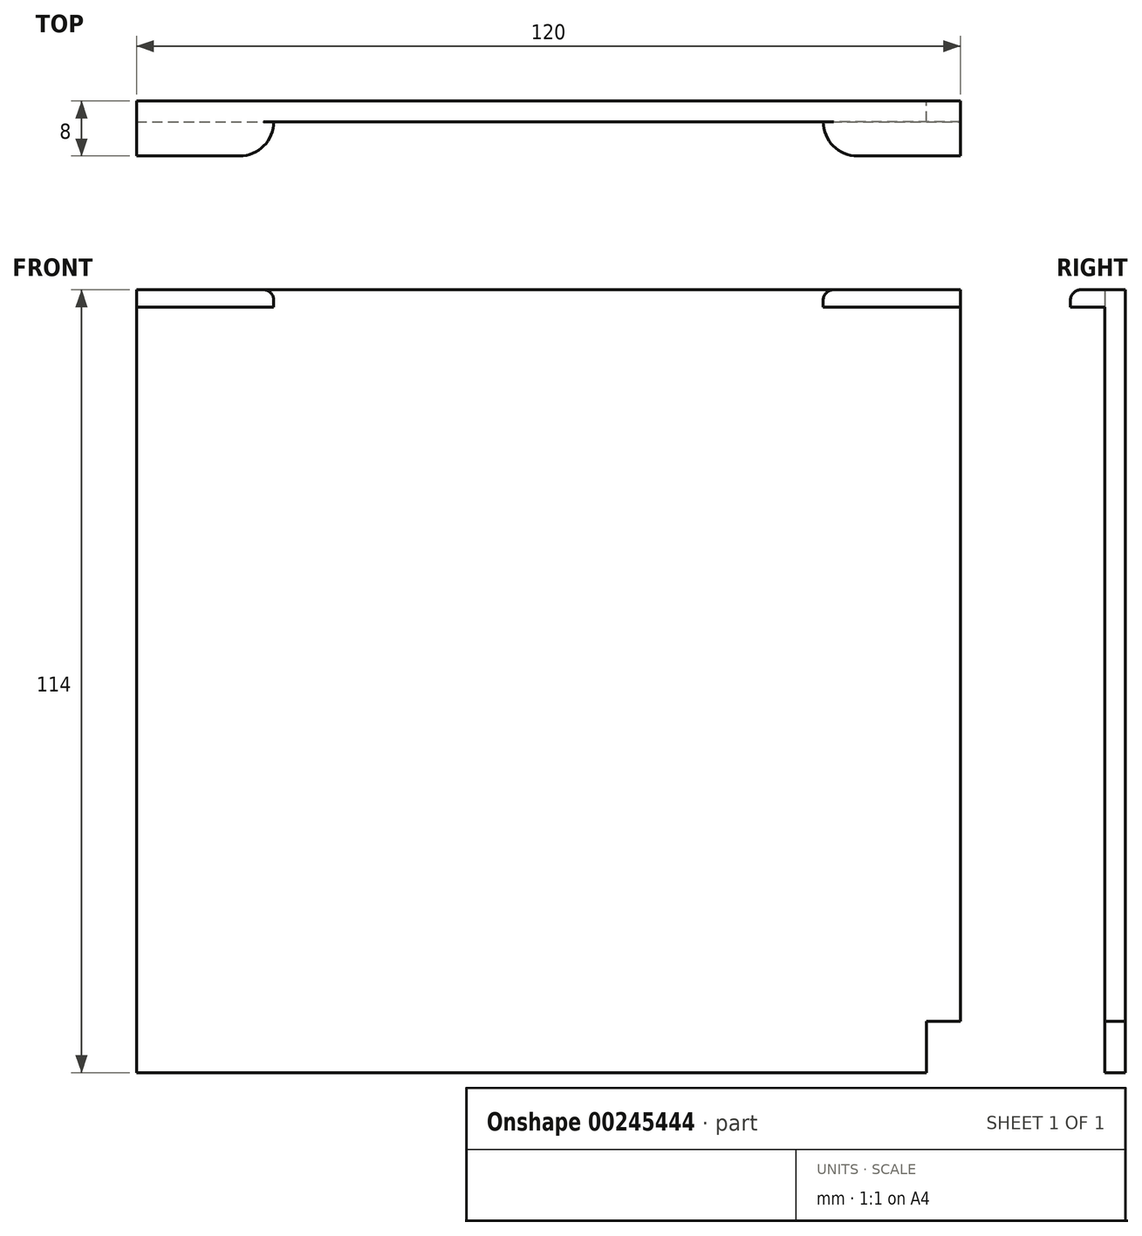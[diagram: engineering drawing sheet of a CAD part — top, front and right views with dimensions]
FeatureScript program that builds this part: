
annotation { "Feature Type Name" : "Feature", "Feature Type Description" : "" }
export const myFeature = defineFeature(function(context is Context, id is Id, definition is map)
    precondition{}
    {
        {
            var Q0;
            Q0=qCreatedBy(makeId("Front.planeOp"),FACE);
            var sketch = newSketch(context, id + "F0", { "sketchPlane" : qUnion([Q0])});
            skLineSegment(sketch, "E0.bottom", {"start": v(0, 0) * mm, "end": v(120, 0) * mm});
            skLineSegment(sketch, "E0.top", {"start": v(0, 114) * mm, "end": v(120, 114) * mm});
            skLineSegment(sketch, "E0.left", {"start": v(0, 0) * mm, "end": v(0, 114) * mm});
            skLineSegment(sketch, "E0.right", {"start": v(120, 0) * mm, "end": v(120, 114) * mm});
            skSolve(sketch);
        }
        {
            var Q0;
            Q0=qSketchRegion(id+"F0",true);
            extrude(context, id + "F1", {"entities" : qUnion([Q0]), "depth" : 3 * mm});
        }
        {
            var Q0;
            Q0=makeQuery(id+"F1.opExtrude","CAP_FACE",FACE,{"disambiguationData":[OSD([sQuery(id+"F0.wireOp",EDGE,"E0.bottom"),sQuery(id+"F0.wireOp",EDGE,"E0.top"),sQuery(id+"F0.wireOp",EDGE,"E0.left"),sQuery(id+"F0.wireOp",EDGE,"E0.right")])],"isStart":false});
            var sketch = newSketch(context, id + "F2", { "sketchPlane" : qUnion([Q0])});
            skLineSegment(sketch, "E1.bottom", {"start": v(0, 114) * mm, "end": v(20, 114) * mm});
            skLineSegment(sketch, "E1.top", {"start": v(0, 111.5) * mm, "end": v(20, 111.5) * mm});
            skLineSegment(sketch, "E1.left", {"start": v(0, 114) * mm, "end": v(0, 111.5) * mm});
            skLineSegment(sketch, "E1.right", {"start": v(20, 114) * mm, "end": v(20, 111.5) * mm});
            skLineSegment(sketch, "E2", {"start": v(60, 114) * mm, "end": v(60, 93.98) * mm});
            skPoint(sketch, "E2.endSnap0", {"position": v(60, 114) * mm});
            skLineSegment(sketch, "E3.MirrorCS", {"start": v(120, 114) * mm, "end": v(100, 114) * mm});
            skLineSegment(sketch, "E4.MirrorCS", {"start": v(120, 111.5) * mm, "end": v(100, 111.5) * mm});
            skLineSegment(sketch, "E5.MirrorCS", {"start": v(100, 114) * mm, "end": v(100, 111.5) * mm});
            skLineSegment(sketch, "E6.MirrorCS", {"start": v(120, 114) * mm, "end": v(120, 111.5) * mm});
            skSolve(sketch);
        }
        {
            var Q0;
            Q0 = qSketchRegion(id + "F2", true);
            extrude(context, id + "F3", {"entities" : qUnion([Q0]), "operationType" : NewBodyOperationType.ADD, "depth" : 5 * mm});
        }
        {
            var Q0;
            Q0=makeQuery(id+"F3.opExtrude","CAP_EDGE",EDGE,{"disambiguationData":[OSD([sQuery(id+"F2.wireOp",EDGE,"E1.right")])],"isStart":false});
            var Q1;
            Q1=makeQuery(id+"F3.opExtrude","CAP_EDGE",EDGE,{"disambiguationData":[OSD([sQuery(id+"F2.wireOp",EDGE,"E5.MirrorCS")])],"isStart":false});
            fillet(context, id + "F4", {"entities" : qUnion([Q0, Q1]), "radius" : 5 * mm, "tangentPropagation" : true, "allowEdgeOverflow" : false});
        }
        {
            var Q0;
            Q0=makeQuery(id+"F3.opExtrude","CAP_EDGE",EDGE,{"disambiguationData":[OSD([sQuery(id+"F2.wireOp",EDGE,"E1.bottom")])],"isStart":false});
            var Q1;
            Q1=makeQuery(id+"F3.opExtrude","CAP_EDGE",EDGE,{"disambiguationData":[OSD([sQuery(id+"F2.wireOp",EDGE,"E3.MirrorCS")])],"isStart":false});
            fillet(context, id + "F5", {"entities" : qUnion([Q0, Q1]), "radius" : 1.5 * mm, "tangentPropagation" : true, "allowEdgeOverflow" : false});
        }
        {
            var Q0;
            Q0=makeQuery(id+"F1.opExtrude","CAP_FACE",FACE,{"disambiguationData":[OSD([sQuery(id+"F0.wireOp",EDGE,"E0.bottom"),sQuery(id+"F0.wireOp",EDGE,"E0.top"),sQuery(id+"F0.wireOp",EDGE,"E0.left"),sQuery(id+"F0.wireOp",EDGE,"E0.right")])],"isStart":true});
            var sketch = newSketch(context, id + "F6", { "sketchPlane" : qUnion([Q0])});
            skLineSegment(sketch, "E7.bottom", {"start": v(-120, 0) * mm, "end": v(-115, 0) * mm});
            skLineSegment(sketch, "E7.top", {"start": v(-120, 7.5) * mm, "end": v(-115, 7.5) * mm});
            skLineSegment(sketch, "E7.left", {"start": v(-120, 0) * mm, "end": v(-120, 7.5) * mm});
            skLineSegment(sketch, "E7.right", {"start": v(-115, 0) * mm, "end": v(-115, 7.5) * mm});
            skSolve(sketch);
        }
        {
            var Q0;
            Q0 = qSketchRegion(id + "F6", true);
            extrude(context, id + "F7", {"entities" : qUnion([Q0]), "operationType" : NewBodyOperationType.REMOVE, "oppositeDirection" : true, "depth" : 25 * mm});
        }
    });
